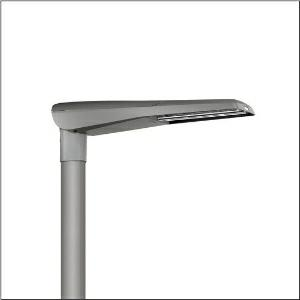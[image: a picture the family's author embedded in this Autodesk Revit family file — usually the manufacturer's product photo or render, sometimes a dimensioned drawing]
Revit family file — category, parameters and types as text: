
# Revit family: streetlight_sl_11_iq_mini___st1_0a_5xc2mc1f08ge_6161
name_source: partatom
category: Lighting Fixtures
units: mm (PartAtom-declared; Revit-internal decimal feet)

## family parameters
Cut with Voids When Loaded = No
Host = Face
Light Source = No
Part Type = Normal
Room Calculation Point = No
Round Connector Dimension = Use Diameter
Shared = No

## types (1)
- --- (1 x LED, 2940 lm, 25.3 W, 2200K)
    Apparent Load = 25 VA
    CIE Flux Codes = 33 66 96 100 100
    Color Rendering = 70
    Color Temperature = 2200K
    Default Elevation = 1800 mm
    Description = Streetlight SL 11 iQ mini, mast luminaire, primary light control with 3 zone facetted reflector, of plastic, silver coated, highly specular, primary optical cover: cover, of PMMA, transparent, light distribution: ST1.0a, light emission: direct distribution, primary light characteristic: asymmetric, installation type: post-top, side-entry, lamps: LED, High Power LED, rated values: 3.460lm | 24,9W | 139lm/W (begin service life); end service life: 3.460lm | 25,7W; at 50% lumin. flux: 1.730lm | 12,8W | 135,2lm/W, colour temperature: 2200/2700/3000/4000K, colour rendering: CRI > 70, light colour: 722/727/730/740, light setting 1 begin service life: 100% | 3.460lm | 24,9W | 139lm/W | 3.000K, light setting 1 end service life: 25,7W, further light settings possible, control: Street-Remote, Auto-Match, Temp-Guard, Lumen-Switch, Night-Set, Smart-Wire, Light-Fading, Desk-Remote (wireless, voltage-free reading and setting of iQ features in the workshop via application-optimized NFC function/RFID function), optimised constant luminous flux control (CLO 2.0), with cable H07RN-F 5x 1.5mm², mains connection: 230..240V, AC, 50/60Hz, connection cable pre-assembled, cable length: 6,5m, luminaire housing, of diecast aluminium, powder-coated, Siteco® metallic grey (DB 702S), please order mast flange separately, inclination adjustable without tools: 0°, 5°, 10°, 15° (post-top) | 0°, -5°, -10°, -15° (side-entry), sealing non-destructively replaceable, multi-level sealing system, length: 736mm, width: 174mm, height: 116mm, mast flange for spigot size: 42mm (side-entry): 5XC10008XM4, 60/48mm (side-entry/post-top): 5XC10108XM2, 76/60mm (side-entry/post-top): 5XC10108XM1, equipment: standard, protection rating (complete): IP66, insulation class (complete): insulation class II (safety insulation), certification: CE, ENEC, ENEC+, VDE, impact resistance: IK10, permissible operating ambient temperature for outdoor applications: -25..+50°C, standard-compliant lighting for roads and squares, Environmental Product Declaration (EPD) tested and certified by an independent institute, packaging unit: 1 piece

Light Distribution: ST1.0a
    Height = 116 mm
    Lamp = 1 x LED
    Lamp Light Flux = 2940 lm
    Lamp Power = 25.3 W
    Lamp count = 1
    Length = 736 mm
    Luminous efficacy = 116 lm/W
    Manufacturer = Siteco
    ModVariant = No
    Model = 5XC2MC1F08GE
    Number of Poles = 1
    OnlyDefault = Yes
    Power Factor = 1
    Product Name = Streetlight SL 11 iQ mini | ST1.0a
    Product group = mast luminaire | pylon top
    ProductGroupID = 6100
    Protection Class = Protection class II
    Protection Degree = IP 66
    RLX_Detail_Level = 1
    RLX_Emergency_Light_Flux = 0 lm
    RLX_Emergency_Type = 0
    RLX_Emergency_Type_DB = No
    RlxData = <blob elided: 52877 chars, md5=64d4e667>
    Socket = socket
    Standby Power = 0 W
    System Light Flux = 2940 lm
    System Power = 25 W
    Type Comments = individual setting: luminous flux: 100 % | dim-lin: 254 | 351 mA
    Type Image = l_1003508.jpg
    URL = http://relux.com
    VarID = @adj_035452
    Voltage = 0 V
    Weight = 0.00 kg
    Width = 174 mm

## geometry (parser evidence)
native form markers: Blend x4, Sweep x11
no freeform markers — native parametric forms only
